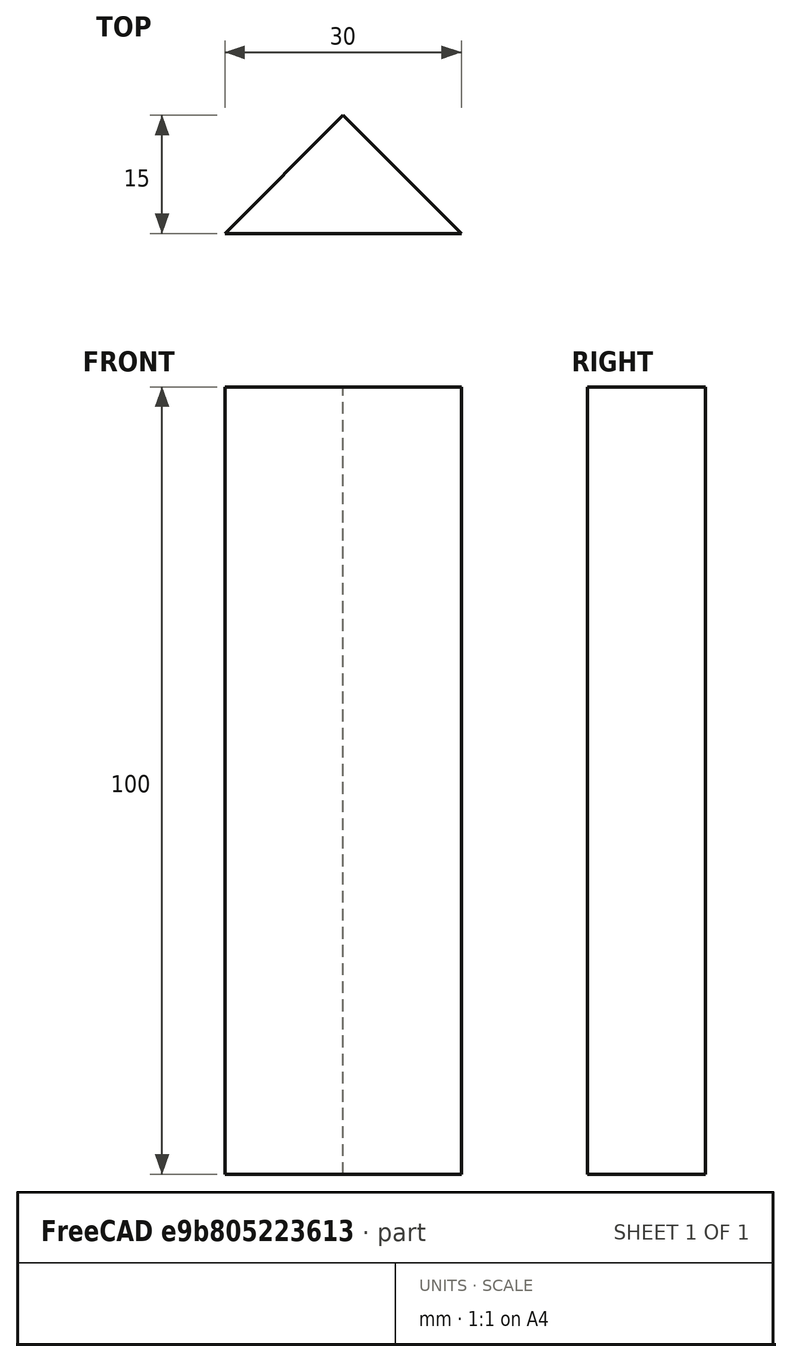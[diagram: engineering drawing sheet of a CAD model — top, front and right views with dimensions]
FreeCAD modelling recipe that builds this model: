
FCSTD DOCUMENT  (FreeCAD 1.0R38806 (Git))
Label: fugura
License: All rights reserved
LicenseURL: https://en.wikipedia.org/wiki/All_rights_reserved
objects: Sketcher::SketchObject×1, Part::Extrusion×1
note: 3 computed .brp shape members not serialized (recipe doc carries the construction recipe); baked Part::Feature solids carry a one-line shape summary decoded from their .brp

FEATURE [Sketcher::SketchObject] Sketch
  ArcFitTolerance = 1e-06
  FullyConstrained = true
  MakeInternals = false
  sketch-geometry (3):
    g0: LineSegment StartX=-15 StartY=0 StartZ=0 EndX=0 EndY=15 EndZ=0
    g1: LineSegment StartX=0 StartY=15 StartZ=0 EndX=15 EndY=0 EndZ=0
    g2: LineSegment StartX=15 StartY=0 StartZ=0 EndX=-15 EndY=0 EndZ=0
  constraints (9):
    c: PointOnObject(g0,g-1)
    c: PointOnObject(g0,g-2)
    c: Coincident(g0,g1)
    c: PointOnObject(g1,g-1)
    c: Coincident(g1,g2)
    c: Coincident(g2,g0)
    c: Equal(g1,g0)
    c: Distance(g2,g2) = 30
    c: Distance(g0,g-1) = 15
FEATURE [Part::Extrusion] Extrude
  Base = -> Sketch
  Dir = (0,0,1)
  DirMode = 2
  FaceMakerClass = Part::FaceMakerBullseye
  FaceMakerMode = 3
  LengthFwd = 100
  LengthRev = 0
  Solid = true
  Symmetric = true
